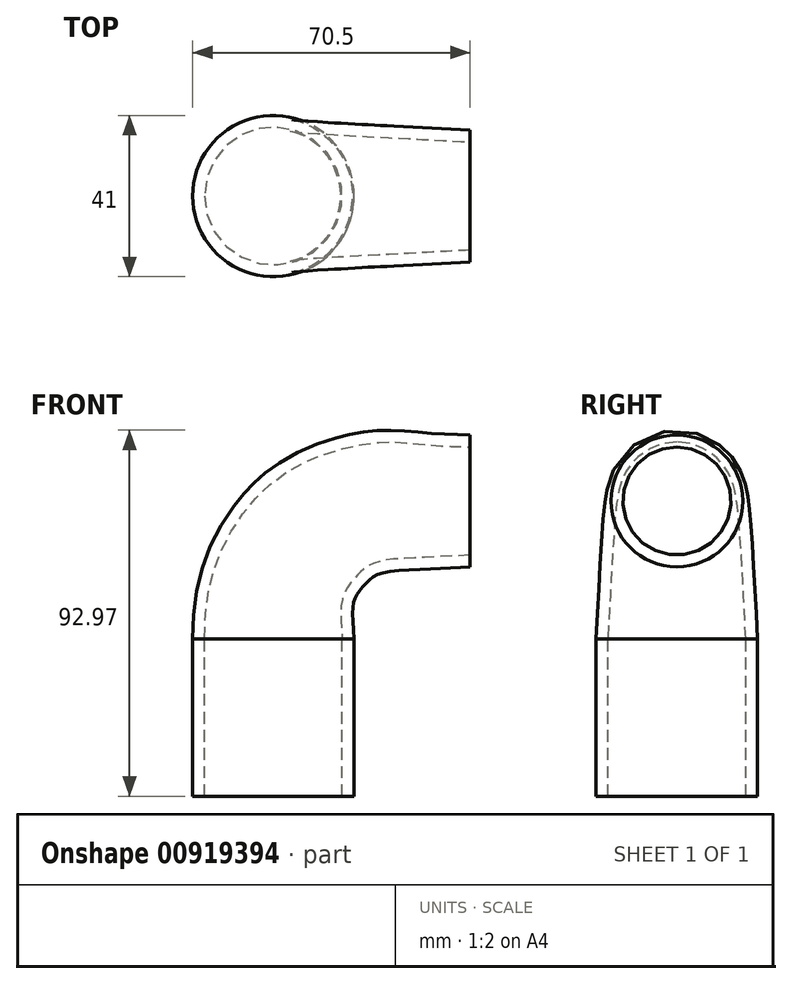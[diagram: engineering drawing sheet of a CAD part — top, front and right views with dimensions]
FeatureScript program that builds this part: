
annotation { "Feature Type Name" : "Feature", "Feature Type Description" : "" }
export const myFeature = defineFeature(function(context is Context, id is Id, definition is map)
    precondition{}
    {
        {
            var Q0;
            Q0=qCreatedBy(makeId("Front.planeOp"),FACE);
            var sketch = newSketch(context, id + "F0", { "sketchPlane" : qUnion([Q0])});
            skLineSegment(sketch, "E0", {"start": v(0, 0) * mm, "end": v(0, 5) * mm});
            skLineSegment(sketch, "E1", {"start": v(30, 35) * mm, "end": v(50, 35) * mm});
            skPoint(sketch, "E2.visualSharp", {"position": v(0, 35) * mm});
            skArc(sketch, "E2.filletArc", {"start": v(30, 35) * mm, "mid": v(8.79, 26.21) * mm, "end": v(0, 5) * mm});
            skSolve(sketch);
        }
        {
            var Q0;
            Q0=sQuery(id+"F0.wireOp",VERTEX,"E1.end");
            var Q1;
            Q1=qCreatedBy(makeId("Right.planeOp"),FACE);
            cPlane(context, id + "F1", {"entities" : qUnion([Q0, Q1]), "cplaneType" : CPlaneType.PLANE_POINT, "offset" : 25 * mm, "width" : 150 * mm, "height" : 150 * mm});
        }
        {
            var Q0;
            Q0=qCreatedBy(id+"F1.planeOp",FACE);
            var sketch = newSketch(context, id + "F2", { "sketchPlane" : qUnion([Q0])});
            skCircle(sketch, "E3", {"center": v(0, 35) * mm, "radius": 16.75 * mm});
            skSolve(sketch);
        }
        {
            var Q0;
            Q0=qCreatedBy(makeId("Top.planeOp"),FACE);
            var sketch = newSketch(context, id + "F3", { "sketchPlane" : qUnion([Q0])});
            skCircle(sketch, "E4", {"center": v(0, 0) * mm, "radius": 20.5 * mm});
            skSolve(sketch);
        }
        {
            var Q0;
            Q0=sQuery(id+"F0.wireOp",EDGE,"E0");
            var Q1;
            Q1=sQuery(id+"F0.wireOp",EDGE,"E2.filletArc");
            var Q2;
            Q2=sQuery(id+"F0.wireOp",EDGE,"E1");
            var Q3;
            Q3=makeQuery(id+"F3.imprint","IMPRINT",FACE,{"disambiguationData":[TD([[makeQuery(id+"F3.imprint","IMPRINT",EDGE,{"derivedFrom":sQuery(id+"F3.wireOp",EDGE,"E4")}),1.0]])]});
            var Q4;
            Q4=makeQuery(id+"F2.imprint","IMPRINT",FACE,{"disambiguationData":[TD([[makeQuery(id+"F2.imprint","IMPRINT",EDGE,{"derivedFrom":sQuery(id+"F2.wireOp",EDGE,"E3")}),1.0]])]});
            loft(context, id + "F4", {"addSections" : true, "spine" : qUnion([Q0, Q1, Q2]), "sectionCount" : 5, "sheetProfilesArray" : [{ "sheetProfileEntities" : qUnion([Q3]) }, { "sheetProfileEntities" : qUnion([Q4]) }]});
        }
        {
            var Q0;
            Q0=makeQuery(id+"F4.opLoft","CAP_FACE",FACE,{"disambiguationData":[OSD([makeQuery(id+"F2.imprint","IMPRINT",FACE,{"disambiguationData":[TD([[makeQuery(id+"F2.imprint","IMPRINT",EDGE,{"derivedFrom":sQuery(id+"F2.wireOp",EDGE,"E3")}),1.0]])]})])],"isStart":true});
            var Q1;
            Q1=makeQuery(id+"F4.opLoft","CAP_FACE",FACE,{"disambiguationData":[OSD([makeQuery(id+"F3.imprint","IMPRINT",FACE,{"disambiguationData":[TD([[makeQuery(id+"F3.imprint","IMPRINT",EDGE,{"derivedFrom":sQuery(id+"F3.wireOp",EDGE,"E4")}),1.0]])]})])],"isStart":true});
            shell(context, id + "F5", {"entities" : qUnion([Q0, Q1]), "thickness" : 3 * mm});
        }
        {
            var Q0;
            Q0=makeQuery(id+"F4.opLoft","CAP_FACE",FACE,{"disambiguationData":[OSD([makeQuery(id+"F3.imprint","IMPRINT",FACE,{"disambiguationData":[TD([[makeQuery(id+"F3.imprint","IMPRINT",EDGE,{"derivedFrom":sQuery(id+"F3.wireOp",EDGE,"E4")}),1.0]])]})])],"isStart":true});
            extrude(context, id + "F6", {"entities" : qUnion([Q0]), "operationType" : NewBodyOperationType.ADD, "depth" : 40 * mm, "offsetDistance" : 25 * mm});
        }
    });
